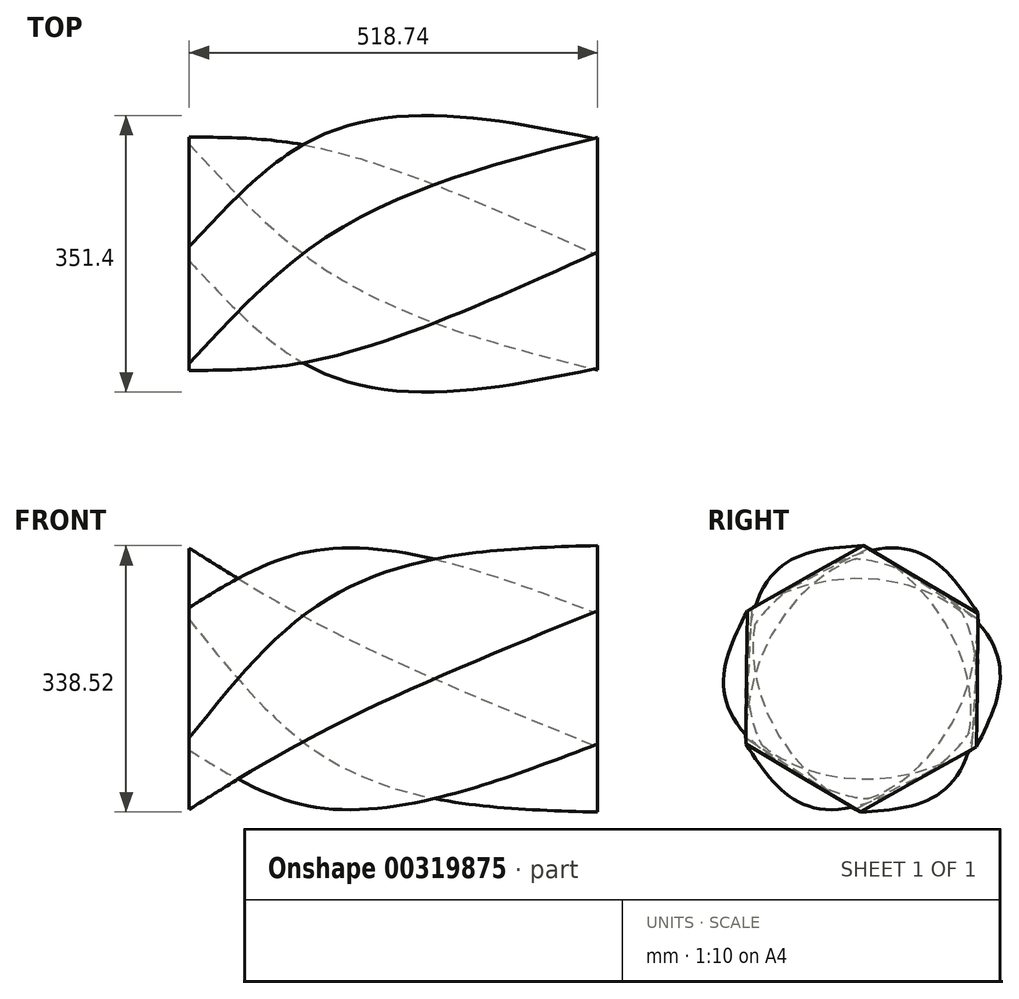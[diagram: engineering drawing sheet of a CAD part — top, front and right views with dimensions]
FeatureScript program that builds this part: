
annotation { "Feature Type Name" : "Feature", "Feature Type Description" : "" }
export const myFeature = defineFeature(function(context is Context, id is Id, definition is map)
    precondition{}
    {
        {
            var Q0;
            Q0=qCreatedBy(makeId("Front.planeOp"),FACE);
            var sketch = newSketch(context, id + "F0", { "sketchPlane" : qUnion([Q0])});
            skLineSegment(sketch, "E0", {"start": v(0, 0) * mm, "end": v(152.09, 0) * mm});
            skSolve(sketch);
        }
        {
            var Q0;
            Q0=sQuery(id+"F0.wireOp",VERTEX,"E0.end");
            var Q1;
            Q1=qCreatedBy(makeId("Right.planeOp"),FACE);
            cPlane(context, id + "F1", {"entities" : qUnion([Q0, Q1]), "cplaneType" : CPlaneType.PLANE_POINT, "offset" : 25 * mm, "width" : 150 * mm, "height" : 150 * mm});
        }
        {
            var Q0;
            Q0=qCreatedBy(makeId("Front.planeOp"),FACE);
            var sketch = newSketch(context, id + "F2", { "sketchPlane" : qUnion([Q0])});
            skLineSegment(sketch, "E1", {"start": v(153.78, 0) * mm, "end": v(518.74, 0) * mm});
            skSolve(sketch);
        }
        {
            var Q0;
            Q0=sQuery(id+"F2.wireOp",VERTEX,"E1.end");
            var Q1;
            Q1=qCreatedBy(id+"F1.planeOp",FACE);
            cPlane(context, id + "F3", {"entities" : qUnion([Q0, Q1]), "cplaneType" : CPlaneType.PLANE_POINT, "offset" : 25 * mm, "width" : 150 * mm, "height" : 150 * mm});
        }
        {
            var Q0;
            Q0=qCreatedBy(makeId("Right.planeOp"),FACE);
            var sketch = newSketch(context, id + "F4", { "sketchPlane" : qUnion([Q0])});
            skCircle(sketch, "E2.cCircle", {"center": v(0, 0) * mm, "radius": 143.87 * mm, "construction": true});
            skLineSegment(sketch, "E2.0", {"start": v(139.22, -90.64) * mm, "end": v(-8.89, -165.9) * mm});
            skLineSegment(sketch, "E2.1", {"start": v(-8.89, -165.9) * mm, "end": v(-148.11, -75.25) * mm});
            skLineSegment(sketch, "E2.2", {"start": v(-148.11, -75.25) * mm, "end": v(-139.22, 90.64) * mm});
            skLineSegment(sketch, "E2.3", {"start": v(-139.22, 90.64) * mm, "end": v(8.89, 165.9) * mm});
            skLineSegment(sketch, "E2.4", {"start": v(8.89, 165.9) * mm, "end": v(148.11, 75.25) * mm});
            skLineSegment(sketch, "E2.5", {"start": v(148.11, 75.25) * mm, "end": v(139.22, -90.64) * mm});
            skPoint(sketch, "E2.0.midPoint", {"position": v(65.17, -128.27) * mm});
            skSolve(sketch);
        }
        {
            var Q0;
            Q0=qCreatedBy(id+"F1.planeOp",FACE);
            var sketch = newSketch(context, id + "F5", { "sketchPlane" : qUnion([Q0])});
            skCircle(sketch, "E3.cCircle", {"center": v(0, 0) * mm, "radius": 140.03 * mm, "construction": true});
            skLineSegment(sketch, "E3.0", {"start": v(137.11, -85.7) * mm, "end": v(-5.66, -161.6) * mm});
            skLineSegment(sketch, "E3.1", {"start": v(-5.66, -161.6) * mm, "end": v(-142.77, -75.9) * mm});
            skLineSegment(sketch, "E3.2", {"start": v(-142.77, -75.9) * mm, "end": v(-137.11, 85.7) * mm});
            skLineSegment(sketch, "E3.3", {"start": v(-137.11, 85.7) * mm, "end": v(5.66, 161.6) * mm});
            skLineSegment(sketch, "E3.4", {"start": v(5.66, 161.6) * mm, "end": v(142.77, 75.9) * mm});
            skLineSegment(sketch, "E3.5", {"start": v(142.77, 75.9) * mm, "end": v(137.11, -85.7) * mm});
            skPoint(sketch, "E3.0.midPoint", {"position": v(65.73, -123.65) * mm});
            skSolve(sketch);
        }
        {
            var Q0;
            Q0=qCreatedBy(id+"F3.planeOp",FACE);
            var sketch = newSketch(context, id + "F6", { "sketchPlane" : qUnion([Q0])});
            skCircle(sketch, "E4.cCircle", {"center": v(0, 0) * mm, "radius": 146.6 * mm, "construction": true});
            skLineSegment(sketch, "E4.0", {"start": v(145.6, -86.34) * mm, "end": v(-1.97, -169.26) * mm});
            skLineSegment(sketch, "E4.1", {"start": v(-1.97, -169.26) * mm, "end": v(-147.57, -82.92) * mm});
            skLineSegment(sketch, "E4.2", {"start": v(-147.57, -82.92) * mm, "end": v(-145.6, 86.34) * mm});
            skLineSegment(sketch, "E4.3", {"start": v(-145.6, 86.34) * mm, "end": v(1.97, 169.26) * mm});
            skLineSegment(sketch, "E4.4", {"start": v(1.97, 169.26) * mm, "end": v(147.57, 82.92) * mm});
            skLineSegment(sketch, "E4.5", {"start": v(147.57, 82.92) * mm, "end": v(145.6, -86.34) * mm});
            skPoint(sketch, "E4.0.midPoint", {"position": v(71.8, -127.8) * mm});
            skSolve(sketch);
        }
        {
            var Q0;
            Q0=makeQuery(id+"F4.imprint","IMPRINT",FACE,{"disambiguationData":[TD([[makeQuery(id+"F4.imprint","IMPRINT",EDGE,{"derivedFrom":sQuery(id+"F4.wireOp",EDGE,"E2.0")}),-1.0]])]});
            var Q1;
            Q1=makeQuery(id+"F5.imprint","IMPRINT",FACE,{"disambiguationData":[TD([[makeQuery(id+"F5.imprint","IMPRINT",EDGE,{"derivedFrom":sQuery(id+"F5.wireOp",EDGE,"E3.0")}),-1.0]])]});
            var Q2;
            Q2=makeQuery(id+"F6.imprint","IMPRINT",FACE,{"disambiguationData":[TD([[makeQuery(id+"F6.imprint","IMPRINT",EDGE,{"derivedFrom":sQuery(id+"F6.wireOp",EDGE,"E4.0")}),-1.0]])]});
            var Q3;
            Q3=sQuery(id+"F5.wireOp",VERTEX,"E3.1.start");
            var Q4;
            Q4=sQuery(id+"F4.wireOp",VERTEX,"E2.5.end");
            var Q5;
            Q5=sQuery(id+"F6.wireOp",VERTEX,"E4.2.start");
            loft(context, id + "F7", {"sheetProfilesArray" : [{ "sheetProfileEntities" : qUnion([Q0]) }, { "sheetProfileEntities" : qUnion([Q1]) }, { "sheetProfileEntities" : qUnion([Q2]) }], "matchConnections" : true, "connections" : [{ "connectionEntities" : qUnion([Q3, Q4, Q5]), "connectionEdgeQueries" : qUnion([]), "connectionEdgeParameters" : [] }]});
        }
    });
